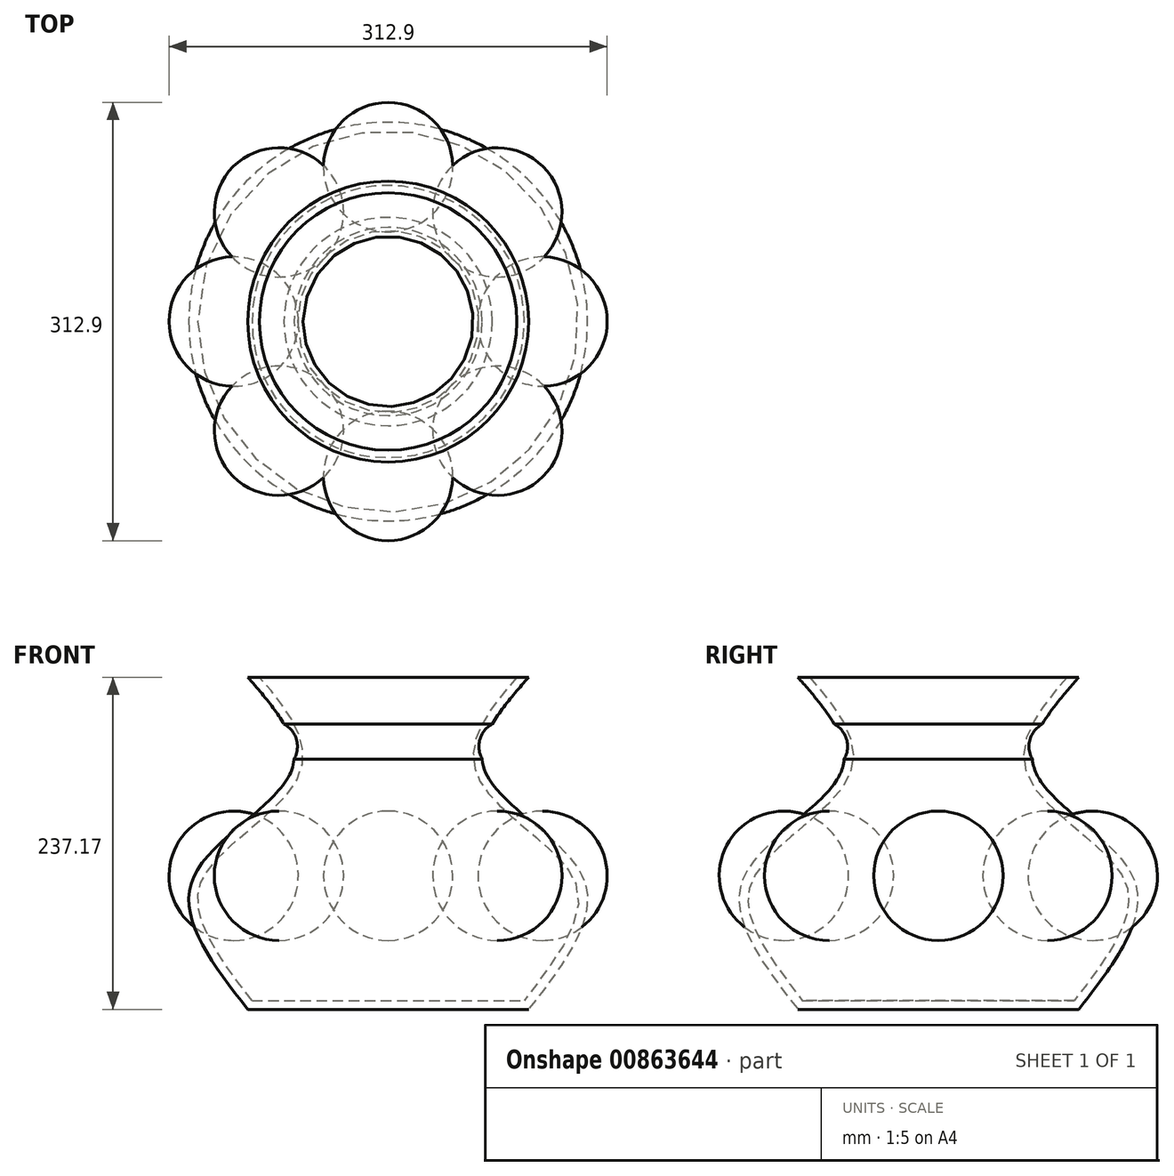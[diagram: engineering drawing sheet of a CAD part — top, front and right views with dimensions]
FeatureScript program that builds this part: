
annotation { "Feature Type Name" : "Feature", "Feature Type Description" : "" }
export const myFeature = defineFeature(function(context is Context, id is Id, definition is map)
    precondition{}
    {
        {
            var Q0;
            Q0=qCreatedBy(makeId("Front.planeOp"),FACE);
            var sketch = newSketch(context, id + "F0", { "sketchPlane" : qUnion([Q0])});
            skLineSegment(sketch, "E0", {"start": v(0, 0) * mm, "end": v(0, 237.17) * mm});
            skLineSegment(sketch, "E1", {"start": v(0, 237.17) * mm, "end": v(100.28, 237.17) * mm});
            skLineSegment(sketch, "E2", {"start": v(0, 0) * mm, "end": v(100.28, 0) * mm});
            skFitSpline(sketch, "E3", {"points": [v(100.28, 0) * mm, v(139.59, 92.92) * mm, v(69, 170.56) * mm, v(100.28, 237.17) * mm], "startDerivative": vector(217.86, 280.25) * mm, "endDerivative": vector(198.9, 228.44) * mm});
            skSolve(sketch);
        }
        {
            var Q0;
            Q0 = qSketchRegion(id + "F0", true);
            var Q1;
            Q1=sQuery(id+"F0.wireOp",EDGE,"E0");
            revolve(context, id + "F1", {"surfaceOperationType" : NewSurfaceOperationType.NEW, "entities" : qUnion([Q0]), "axis" : qUnion([Q1]), "revolveType" : RevolveType.FULL});
        }
        {
            var Q0;
            Q0=qCreatedBy(makeId("Right.planeOp"),FACE);
            var sketch = newSketch(context, id + "F2", { "sketchPlane" : qUnion([Q0])});
            skArc(sketch, "E4", {"start": v(-465.89, 268.94) * mm, "mid": v(-419.72, 315.1) * mm, "end": v(-465.89, 361.27) * mm});
            skLineSegment(sketch, "E5", {"start": v(-465.89, 361.27) * mm, "end": v(-465.89, 268.94) * mm});
            skSolve(sketch);
        }
        {
            var Q0;
            Q0 = qSketchRegion(id + "F2", true);
            var Q1;
            Q1=sQuery(id+"F2.wireOp",EDGE,"E5");
            revolve(context, id + "F3", {"surfaceOperationType" : NewSurfaceOperationType.NEW, "entities" : qUnion([Q0]), "axis" : qUnion([Q1]), "revolveType" : RevolveType.FULL});
        }
        {
            var Q0;
            Q0=makeQuery(id+"F3.opRevolve","SWEPT_BODY",BODY,{"disambiguationData":[OSD([sQuery(id+"F2.wireOp",EDGE,"E4"),sQuery(id+"F2.wireOp",EDGE,"E5")])]});
            transform(context, id + "F4", {"entities" : qUnion([Q0]), "transformType" : TransformType.TRANSLATION_3D, "dx" : 0 * mm, "dy" : 355.6 * mm, "dz" : -219.7 * mm, "makeCopy" : false});
        }
        {
            var Q0;
            Q0=makeQuery(id+"F3.opRevolve","SWEPT_BODY",BODY,{"disambiguationData":[OSD([sQuery(id+"F2.wireOp",EDGE,"E4"),sQuery(id+"F2.wireOp",EDGE,"E5")])]});
            var Q1;
            Q1=makeQuery(id+"F1.opRevolve","SWEPT_EDGE",EDGE,{"disambiguationData":[OSD([sQuery(id+"F0.wireOp",EDGE,"E1"),sQuery(id+"F0.wireOp",EDGE,"E3")])]});
            circularPattern(context, id + "F5", {"entities" : qUnion([Q0]), "axis" : qUnion([Q1]), "angle" : 360 * degree, "instanceCount" : 8, "equalSpace" : true});
        }
        {
            var Q0;
            Q0=makeQuery(id+"F1.opRevolve","SWEPT_FACE",FACE,{"disambiguationData":[OSD([sQuery(id+"F0.wireOp",EDGE,"E1")])]});
            shell(context, id + "F6", {"entities" : qUnion([Q0]), "thickness" : 6.35 * mm});
        }
        {
            var Q0;
            Q0=qCreatedBy(makeId("Front.planeOp"),FACE);
            var sketch = newSketch(context, id + "F7", { "sketchPlane" : qUnion([Q0])});
            skCircle(sketch, "E6", {"center": v(-82.87, 187.71) * mm, "radius": 18.1 * mm});
            skSolve(sketch);
        }
        {
            var Q0;
            Q0 = qSketchRegion(id + "F7", true);
            var Q1;
            Q1=makeQuery(id+"F1.opRevolve","SWEPT_EDGE",EDGE,{"disambiguationData":[OSD([sQuery(id+"F0.wireOp",EDGE,"E1"),sQuery(id+"F0.wireOp",EDGE,"E3")])]});
            revolve(context, id + "F8", {"operationType" : NewBodyOperationType.REMOVE, "surfaceOperationType" : NewSurfaceOperationType.NEW, "entities" : qUnion([Q0]), "axis" : qUnion([Q1]), "revolveType" : RevolveType.FULL});
        }
        {
            var Q0;
            Q0=qCreatedBy(makeId("Front.planeOp"),FACE);
            var sketch = newSketch(context, id + "F9", { "sketchPlane" : qUnion([Q0])});
            skArc(sketch, "E7", {"start": v(176.78, 227.36) * mm, "mid": v(157.46, 208.04) * mm, "end": v(176.78, 188.7) * mm});
            skLineSegment(sketch, "E8", {"start": v(176.78, 227.36) * mm, "end": v(176.78, 188.7) * mm});
            skSolve(sketch);
        }
        {
            var Q0;
            Q0 = qSketchRegion(id + "F9", true);
            var Q1;
            Q1=sQuery(id+"F9.wireOp",EDGE,"E8");
            revolve(context, id + "F10", {"surfaceOperationType" : NewSurfaceOperationType.NEW, "entities" : qUnion([Q0]), "axis" : qUnion([Q1]), "revolveType" : RevolveType.FULL});
        }
        {
            var Q0;
            Q0=makeQuery(id+"F10.opRevolve","SWEPT_BODY",BODY,{"disambiguationData":[OSD([sQuery(id+"F9.wireOp",EDGE,"E7"),sQuery(id+"F9.wireOp",EDGE,"E8")])]});
            transform(context, id + "F11", {"entities" : qUnion([Q0]), "transformType" : TransformType.TRANSLATION_3D, "dx" : -86.61 * mm, "dy" : 0 * mm, "dz" : 8.13 * mm, "makeCopy" : false});
        }
        {
            var Q0;
            Q0=makeQuery(id+"F10.opRevolve","SWEPT_BODY",BODY,{"disambiguationData":[OSD([sQuery(id+"F9.wireOp",EDGE,"E7"),sQuery(id+"F9.wireOp",EDGE,"E8")])]});
            var Q1;
            Q1=makeQuery(id+"F1.opRevolve","SWEPT_EDGE",EDGE,{"disambiguationData":[OSD([sQuery(id+"F0.wireOp",EDGE,"E1"),sQuery(id+"F0.wireOp",EDGE,"E3")])]});
            circularPattern(context, id + "F12", {"entities" : qUnion([Q0]), "axis" : qUnion([Q1]), "angle" : 360 * degree, "instanceCount" : 6, "equalSpace" : true});
        }
        {
            var Q0;
            Q0=makeQuery(id+"F12.opPattern","COPY",BODY,{"derivedFrom":makeQuery(id+"F10.opRevolve","SWEPT_BODY",BODY,{"disambiguationData":[OSD([sQuery(id+"F9.wireOp",EDGE,"E7"),sQuery(id+"F9.wireOp",EDGE,"E8")])]}),"instanceName":"2"});
            var Q1;
            Q1=makeQuery(id+"F12.opPattern","COPY",BODY,{"derivedFrom":makeQuery(id+"F10.opRevolve","SWEPT_BODY",BODY,{"disambiguationData":[OSD([sQuery(id+"F9.wireOp",EDGE,"E7"),sQuery(id+"F9.wireOp",EDGE,"E8")])]}),"instanceName":"3"});
            var Q2;
            Q2=makeQuery(id+"F12.opPattern","COPY",BODY,{"derivedFrom":makeQuery(id+"F10.opRevolve","SWEPT_BODY",BODY,{"disambiguationData":[OSD([sQuery(id+"F9.wireOp",EDGE,"E7"),sQuery(id+"F9.wireOp",EDGE,"E8")])]}),"instanceName":"1"});
            var Q3;
            Q3=makeQuery(id+"F10.opRevolve","SWEPT_BODY",BODY,{"disambiguationData":[OSD([sQuery(id+"F9.wireOp",EDGE,"E7"),sQuery(id+"F9.wireOp",EDGE,"E8")])]});
            var Q4;
            Q4=makeQuery(id+"F12.opPattern","COPY",BODY,{"derivedFrom":makeQuery(id+"F10.opRevolve","SWEPT_BODY",BODY,{"disambiguationData":[OSD([sQuery(id+"F9.wireOp",EDGE,"E7"),sQuery(id+"F9.wireOp",EDGE,"E8")])]}),"instanceName":"5"});
            var Q5;
            Q5=makeQuery(id+"F12.opPattern","COPY",BODY,{"derivedFrom":makeQuery(id+"F10.opRevolve","SWEPT_BODY",BODY,{"disambiguationData":[OSD([sQuery(id+"F9.wireOp",EDGE,"E7"),sQuery(id+"F9.wireOp",EDGE,"E8")])]}),"instanceName":"4"});
            var Q6;
            Q6=makeQuery(id+"F5.opPattern","COPY",BODY,{"derivedFrom":makeQuery(id+"F3.opRevolve","SWEPT_BODY",BODY,{"disambiguationData":[OSD([sQuery(id+"F2.wireOp",EDGE,"E4"),sQuery(id+"F2.wireOp",EDGE,"E5")])]}),"instanceName":"3"});
            booleanBodies(context, id + "F13", {"operationType" : BooleanOperationType.SUBTRACTION, "tools" : qUnion([Q0, Q1, Q2, Q3, Q4, Q5]), "targets" : qUnion([Q6])});
        }
    });
